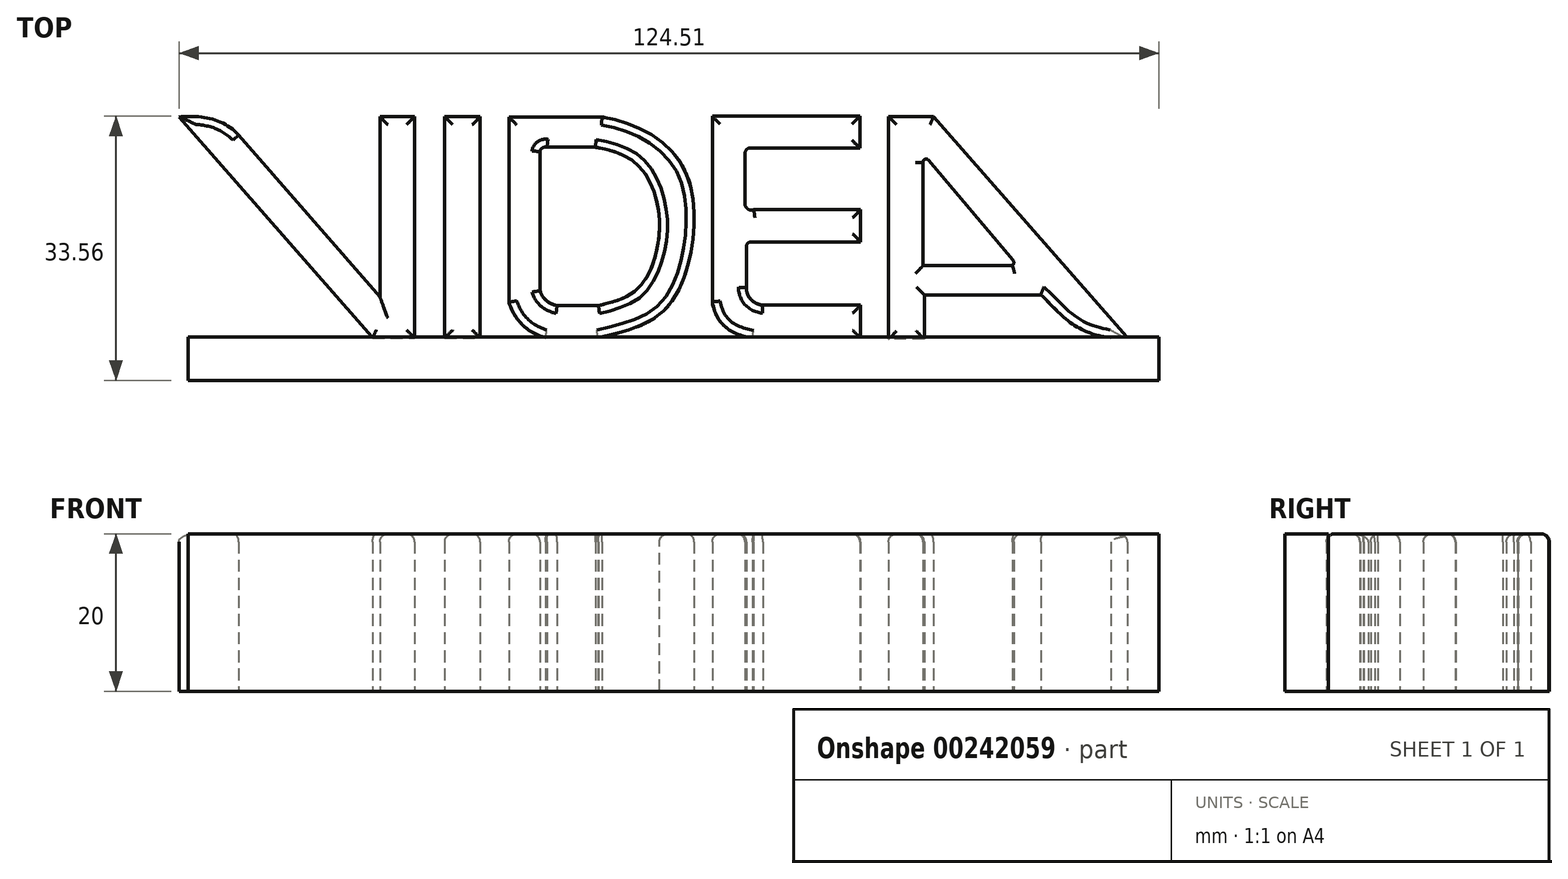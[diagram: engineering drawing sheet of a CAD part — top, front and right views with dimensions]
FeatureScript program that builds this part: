
annotation { "Feature Type Name" : "Feature", "Feature Type Description" : "" }
export const myFeature = defineFeature(function(context is Context, id is Id, definition is map)
    precondition{}
    {
        {
            var Q0;
            Q0=qCreatedBy(makeId("Top.planeOp"),FACE);
            var sketch = newSketch(context, id + "F0", { "sketchPlane" : qUnion([Q0])});
            skLineSegment(sketch, "E0", {"start": v(-62.85, 22.07) * mm, "end": v(-38.24, -5.99) * mm});
            skLineSegment(sketch, "E1", {"start": v(-38.24, -5.99) * mm, "end": v(-32.92, -5.99) * mm});
            skLineSegment(sketch, "E2", {"start": v(-32.92, -5.99) * mm, "end": v(-32.92, 22.12) * mm});
            skLineSegment(sketch, "E3", {"start": v(-32.92, 22.12) * mm, "end": v(-37.3, 22.12) * mm});
            skLineSegment(sketch, "E4", {"start": v(-37.3, 22.12) * mm, "end": v(-37.3, -0.81) * mm});
            skLineSegment(sketch, "E5", {"start": v(-37.3, -0.81) * mm, "end": v(-55.26, 19.8) * mm});
            skFitSpline(sketch, "E6", {"points": [v(-62.85, 22.07) * mm, v(-55.26, 19.8) * mm], "startDerivative": vector(9.47, 0.89) * mm, "endDerivative": vector(5.77, -5.92) * mm});
            skLineSegment(sketch, "E7.bottom", {"start": v(-29.07, 22.12) * mm, "end": v(-24.59, 22.12) * mm});
            skLineSegment(sketch, "E7.top", {"start": v(-29.07, -5.99) * mm, "end": v(-24.59, -5.99) * mm});
            skLineSegment(sketch, "E7.left", {"start": v(-29.07, 22.12) * mm, "end": v(-29.07, -5.99) * mm});
            skLineSegment(sketch, "E7.right", {"start": v(-24.59, 22.12) * mm, "end": v(-24.59, -5.99) * mm});
            skLineSegment(sketch, "E8", {"start": v(-20.94, -1.45) * mm, "end": v(-20.94, 22.07) * mm});
            skLineSegment(sketch, "E9", {"start": v(-20.94, 22.07) * mm, "end": v(-9.1, 22.07) * mm});
            skLineSegment(sketch, "E10", {"start": v(-17, 17.68) * mm, "end": v(-17, 0) * mm});
            skLineSegment(sketch, "E11", {"start": v(-16.1, 18.22) * mm, "end": v(-9.94, 18.22) * mm});
            skLineSegment(sketch, "E12", {"start": v(-14.82, -1.9) * mm, "end": v(-9.55, -1.9) * mm});
            skFitSpline(sketch, "E13", {"points": [v(-9.1, 22.07) * mm, v(0.46, 16.84) * mm, v(2.58, 8.46) * mm, v(-0.52, -1.75) * mm, v(-9.64, -5.99) * mm], "startDerivative": vector(49.9, -8.5) * mm, "endDerivative": vector(-52.09, -11.84) * mm});
            skLineSegment(sketch, "E14", {"start": v(-9.64, -5.99) * mm, "end": v(-16.27, -5.99) * mm});
            skFitSpline(sketch, "E15", {"points": [v(-20.94, -1.45) * mm, v(-16.27, -5.99) * mm], "startDerivative": vector(2.07, -6.5) * mm, "endDerivative": vector(7.54, -2.22) * mm});
            skFitSpline(sketch, "E16", {"points": [v(-17, 0) * mm, v(-14.82, -1.9) * mm], "startDerivative": vector(1.03, -3.03) * mm, "endDerivative": vector(3.55, -0.89) * mm});
            skFitSpline(sketch, "E17", {"points": [v(-17, 17.68) * mm, v(-16.1, 18.22) * mm], "startDerivative": vector(0.15, 1.04) * mm, "endDerivative": vector(1.33, -0.44) * mm});
            skFitSpline(sketch, "E18", {"points": [v(-9.94, 18.22) * mm, v(-3.87, 15.16) * mm, v(-1.8, 8.6) * mm, v(-3.78, 1.16) * mm, v(-9.55, -1.9) * mm], "startDerivative": vector(38.28, -6.58) * mm, "endDerivative": vector(-38.51, -9.17) * mm});
            skLineSegment(sketch, "E19", {"start": v(9.74, 18.12) * mm, "end": v(23.64, 18.12) * mm});
            skLineSegment(sketch, "E20", {"start": v(23.64, 18.12) * mm, "end": v(23.64, 22.17) * mm});
            skLineSegment(sketch, "E21", {"start": v(23.64, 22.17) * mm, "end": v(4.9, 22.17) * mm});
            skLineSegment(sketch, "E22", {"start": v(4.9, 22.17) * mm, "end": v(4.9, -1.4) * mm});
            skLineSegment(sketch, "E23", {"start": v(9.04, 17.43) * mm, "end": v(9.04, 11.07) * mm});
            skLineSegment(sketch, "E24", {"start": v(10.17, 10.28) * mm, "end": v(23.74, 10.28) * mm});
            skLineSegment(sketch, "E25", {"start": v(23.74, 10.28) * mm, "end": v(23.74, 6.19) * mm});
            skLineSegment(sketch, "E26", {"start": v(23.74, 6.19) * mm, "end": v(9.78, 6.19) * mm});
            skLineSegment(sketch, "E27", {"start": v(9.24, 5.65) * mm, "end": v(9.24, 0.42) * mm});
            skLineSegment(sketch, "E28", {"start": v(11.31, -1.85) * mm, "end": v(23.74, -1.85) * mm});
            skLineSegment(sketch, "E29", {"start": v(23.74, -1.85) * mm, "end": v(23.74, -6.04) * mm});
            skLineSegment(sketch, "E30", {"start": v(23.74, -6.04) * mm, "end": v(10.03, -6.04) * mm});
            skFitSpline(sketch, "E31", {"points": [v(4.9, -1.4) * mm, v(10.03, -6.04) * mm], "startDerivative": vector(1.63, -10.06) * mm, "endDerivative": vector(6.8, -1.33) * mm});
            skFitSpline(sketch, "E32", {"points": [v(9.24, 0.42) * mm, v(11.31, -1.85) * mm], "startDerivative": vector(-0.15, -3.85) * mm, "endDerivative": vector(3.4, -0.44) * mm});
            skArc(sketch, "E33", {"start": v(9.74, 18.12) * mm, "mid": v(9.25, 17.92) * mm, "end": v(9.04, 17.43) * mm});
            skArc(sketch, "E34", {"start": v(9.04, 11.07) * mm, "mid": v(9.4, 10.39) * mm, "end": v(10.17, 10.28) * mm});
            skArc(sketch, "E35", {"start": v(9.78, 6.19) * mm, "mid": v(9.4, 6.03) * mm, "end": v(9.24, 5.65) * mm});
            skLineSegment(sketch, "E36", {"start": v(46.62, -0.52) * mm, "end": v(31.83, -0.52) * mm});
            skLineSegment(sketch, "E37", {"start": v(31.83, -0.52) * mm, "end": v(31.83, -6.14) * mm});
            skLineSegment(sketch, "E38", {"start": v(31.83, -6.14) * mm, "end": v(27.3, -6.14) * mm});
            skLineSegment(sketch, "E39", {"start": v(27.3, -6.14) * mm, "end": v(27.3, 22.12) * mm});
            skLineSegment(sketch, "E40", {"start": v(27.3, 22.12) * mm, "end": v(33.01, 22.12) * mm});
            skLineSegment(sketch, "E41", {"start": v(33.01, 22.12) * mm, "end": v(57.66, -5.99) * mm});
            skLineSegment(sketch, "E42", {"start": v(57.66, -5.99) * mm, "end": v(55.56, -5.99) * mm});
            skLineSegment(sketch, "E43", {"start": v(43.02, 3.18) * mm, "end": v(31.68, 3.18) * mm});
            skLineSegment(sketch, "E44", {"start": v(31.68, 3.18) * mm, "end": v(31.68, 16.3) * mm});
            skLineSegment(sketch, "E45", {"start": v(32.37, 16.6) * mm, "end": v(43.07, 3.92) * mm});
            skArc(sketch, "E46", {"start": v(32.37, 16.6) * mm, "mid": v(31.91, 16.7) * mm, "end": v(31.68, 16.3) * mm});
            skArc(sketch, "E47", {"start": v(43.02, 3.18) * mm, "mid": v(43.2, 3.54) * mm, "end": v(43.07, 3.92) * mm});
            skFitSpline(sketch, "E48", {"points": [v(46.62, -0.52) * mm, v(55.56, -5.99) * mm], "startDerivative": vector(7.7, -7.1) * mm, "endDerivative": vector(14.65, -1.92) * mm});
            skSolve(sketch);
        }
        {
            var Q0;
            Q0 = qSketchRegion(id + "F0", true);
            extrude(context, id + "F1", {"entities" : qUnion([Q0]), "depth" : 20 * mm});
        }
        {
            var Q0;
            Q0=makeQuery(id+"F1.opExtrude","CAP_FACE",FACE,{"disambiguationData":[OSD([sQuery(id+"F0.wireOp",EDGE,"E0"),sQuery(id+"F0.wireOp",EDGE,"E1"),sQuery(id+"F0.wireOp",EDGE,"E2"),sQuery(id+"F0.wireOp",EDGE,"E3"),sQuery(id+"F0.wireOp",EDGE,"E4"),sQuery(id+"F0.wireOp",EDGE,"E5"),sQuery(id+"F0.wireOp",EDGE,"E6")])],"isStart":false});
            var Q1;
            Q1=makeQuery(id+"F1.opExtrude","CAP_FACE",FACE,{"disambiguationData":[OSD([sQuery(id+"F0.wireOp",EDGE,"E7.bottom"),sQuery(id+"F0.wireOp",EDGE,"E7.top"),sQuery(id+"F0.wireOp",EDGE,"E7.left"),sQuery(id+"F0.wireOp",EDGE,"E7.right")])],"isStart":false});
            var Q2;
            Q2=makeQuery(id+"F1.opExtrude","CAP_FACE",FACE,{"disambiguationData":[OSD([sQuery(id+"F0.wireOp",EDGE,"E8"),sQuery(id+"F0.wireOp",EDGE,"E9"),sQuery(id+"F0.wireOp",EDGE,"E10"),sQuery(id+"F0.wireOp",EDGE,"E11"),sQuery(id+"F0.wireOp",EDGE,"E12"),sQuery(id+"F0.wireOp",EDGE,"E13"),sQuery(id+"F0.wireOp",EDGE,"E14"),sQuery(id+"F0.wireOp",EDGE,"E15"),sQuery(id+"F0.wireOp",EDGE,"E16"),sQuery(id+"F0.wireOp",EDGE,"E17"),sQuery(id+"F0.wireOp",EDGE,"E18")])],"isStart":false});
            var Q3;
            Q3=makeQuery(id+"F1.opExtrude","CAP_FACE",FACE,{"disambiguationData":[OSD([sQuery(id+"F0.wireOp",EDGE,"E19"),sQuery(id+"F0.wireOp",EDGE,"E20"),sQuery(id+"F0.wireOp",EDGE,"E21"),sQuery(id+"F0.wireOp",EDGE,"E22"),sQuery(id+"F0.wireOp",EDGE,"E23"),sQuery(id+"F0.wireOp",EDGE,"E24"),sQuery(id+"F0.wireOp",EDGE,"E25"),sQuery(id+"F0.wireOp",EDGE,"E26"),sQuery(id+"F0.wireOp",EDGE,"E27"),sQuery(id+"F0.wireOp",EDGE,"E28"),sQuery(id+"F0.wireOp",EDGE,"E29"),sQuery(id+"F0.wireOp",EDGE,"E30"),sQuery(id+"F0.wireOp",EDGE,"E31"),sQuery(id+"F0.wireOp",EDGE,"E32"),sQuery(id+"F0.wireOp",EDGE,"E33"),sQuery(id+"F0.wireOp",EDGE,"E34"),sQuery(id+"F0.wireOp",EDGE,"E35")])],"isStart":false});
            var Q4;
            Q4=makeQuery(id+"F1.opExtrude","CAP_FACE",FACE,{"disambiguationData":[OSD([sQuery(id+"F0.wireOp",EDGE,"E36"),sQuery(id+"F0.wireOp",EDGE,"E37"),sQuery(id+"F0.wireOp",EDGE,"E38"),sQuery(id+"F0.wireOp",EDGE,"E39"),sQuery(id+"F0.wireOp",EDGE,"E40"),sQuery(id+"F0.wireOp",EDGE,"E41"),sQuery(id+"F0.wireOp",EDGE,"E42"),sQuery(id+"F0.wireOp",EDGE,"E43"),sQuery(id+"F0.wireOp",EDGE,"E44"),sQuery(id+"F0.wireOp",EDGE,"E45"),sQuery(id+"F0.wireOp",EDGE,"E46"),sQuery(id+"F0.wireOp",EDGE,"E47"),sQuery(id+"F0.wireOp",EDGE,"E48")])],"isStart":false});
            fillet(context, id + "F2", {"entities" : qUnion([Q0, Q1, Q2, Q3, Q4]), "radius" : 1 * mm, "tangentPropagation" : true, "allowEdgeOverflow" : false});
        }
        {
            var Q0;
            Q0=qCreatedBy(makeId("Top.planeOp"),FACE);
            var sketch = newSketch(context, id + "F3", { "sketchPlane" : qUnion([Q0])});
            skLineSegment(sketch, "E49.bottom", {"start": v(61.66, -11.4) * mm, "end": v(-61.66, -11.4) * mm});
            skLineSegment(sketch, "E49.top", {"start": v(61.66, -5.9) * mm, "end": v(-61.66, -5.9) * mm});
            skLineSegment(sketch, "E49.left", {"start": v(61.66, -11.4) * mm, "end": v(61.66, -5.9) * mm});
            skLineSegment(sketch, "E49.right", {"start": v(-61.66, -11.4) * mm, "end": v(-61.66, -5.9) * mm});
            skPoint(sketch, "E49.middle", {"position": v(0, -8.64) * mm});
            skSolve(sketch);
        }
        {
            var Q0;
            Q0 = qSketchRegion(id + "F3", true);
            extrude(context, id + "F4", {"entities" : qUnion([Q0]), "depth" : 20 * mm});
        }
    });
